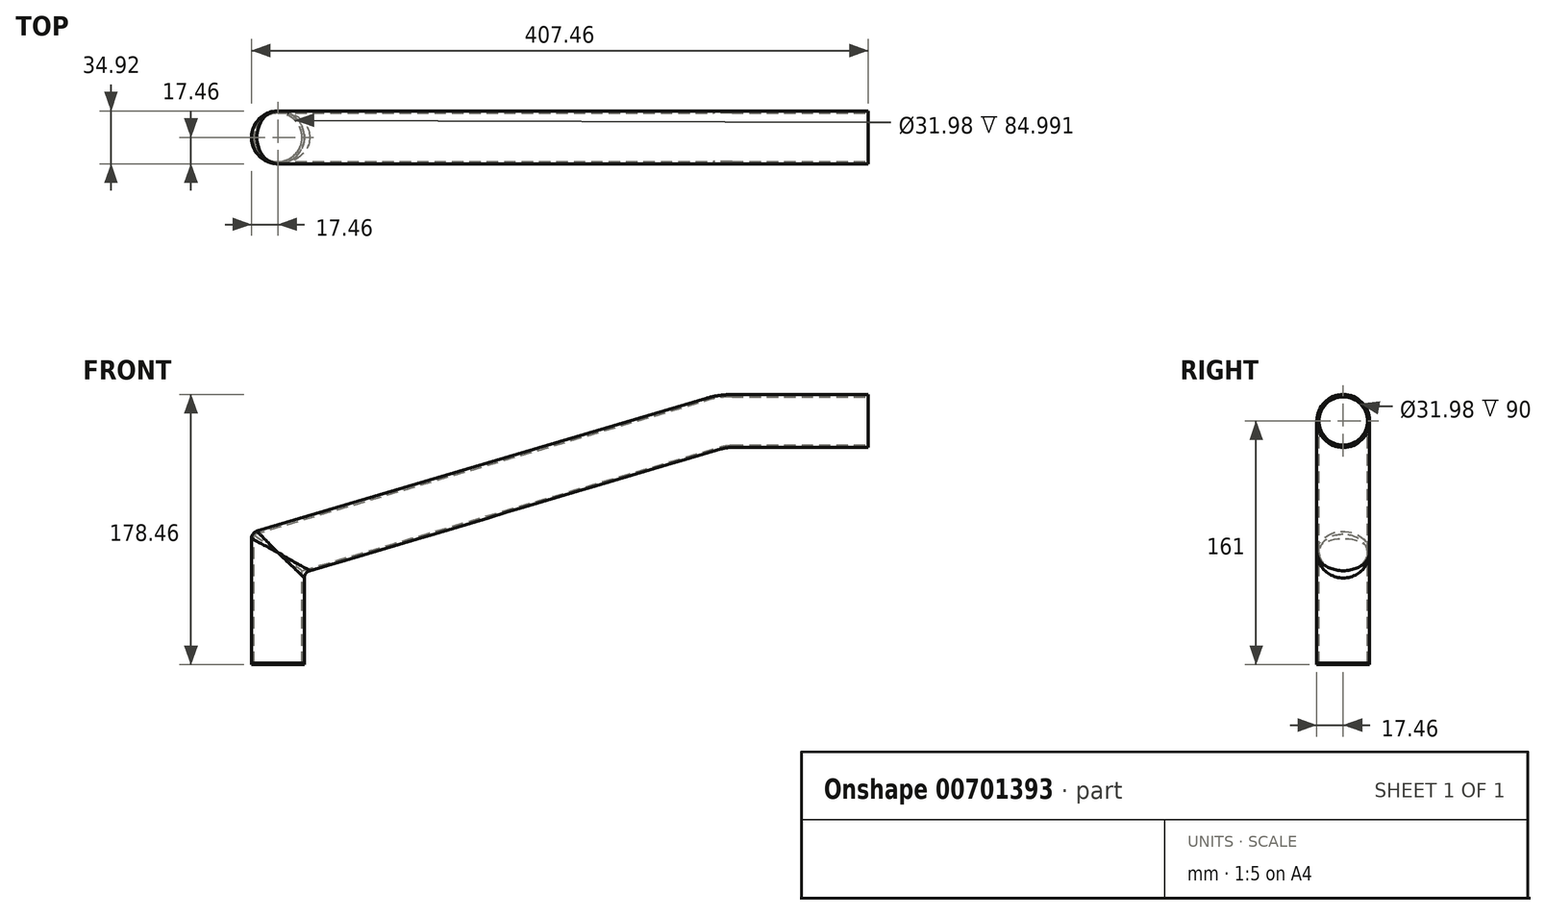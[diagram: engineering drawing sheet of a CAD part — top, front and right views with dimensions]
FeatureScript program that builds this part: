
annotation { "Feature Type Name" : "Feature", "Feature Type Description" : "" }
export const myFeature = defineFeature(function(context is Context, id is Id, definition is map)
    precondition{}
    {
        {
            var Q0;
            Q0=qCreatedBy(makeId("Front.planeOp"),FACE);
            var sketch = newSketch(context, id + "F0", { "sketchPlane" : qUnion([Q0])});
            skLineSegment(sketch, "E0", {"start": v(0, 0) * mm, "end": v(0, 73.04) * mm});
            skLineSegment(sketch, "E1", {"start": v(300, 160) * mm, "end": v(390, 160) * mm});
            skPoint(sketch, "E2.visualSharp", {"position": v(0, 160) * mm});
            skLineSegment(sketch, "E3", {"start": v(287.84, 158.24) * mm, "end": v(0, 73.04) * mm});
            skPoint(sketch, "E4.visualSharp", {"position": v(0, 73.04) * mm});
            skPoint(sketch, "E5.visualSharp", {"position": v(293.79, 160) * mm});
            skArc(sketch, "E5.filletArc", {"start": v(300, 160) * mm, "mid": v(293.85, 159.56) * mm, "end": v(287.84, 158.24) * mm});
            skLineSegment(sketch, "E6", {"start": v(293.79, 160) * mm, "end": v(0, 160) * mm, "construction": true});
            skLineSegment(sketch, "E7", {"start": v(0, 73.04) * mm, "end": v(0, 160) * mm, "construction": true});
            skLineSegment(sketch, "E8.0", {"start": v(17.46, 0) * mm, "end": v(17.46, 60) * mm});
            skLineSegment(sketch, "E8.1", {"start": v(300, 142.54) * mm, "end": v(390, 142.54) * mm});
            skArc(sketch, "E8.2", {"start": v(300, 142.54) * mm, "mid": v(296.36, 142.28) * mm, "end": v(292.8, 141.5) * mm});
            skLineSegment(sketch, "E8.3", {"start": v(292.8, 141.5) * mm, "end": v(17.46, 60) * mm});
            skSolve(sketch);
        }
        {
            var Q0;
            Q0=qCreatedBy(makeId("Top.planeOp"),FACE);
            var sketch = newSketch(context, id + "F1", { "sketchPlane" : qUnion([Q0])});
            skCircle(sketch, "E9", {"center": v(0, 0) * mm, "radius": 15.99 * mm});
            skCircle(sketch, "E10", {"center": v(0, 0) * mm, "radius": 17.46 * mm});
            skSolve(sketch);
        }
        {
            var Q0;
            Q0=makeQuery(id+"F1.imprint","IMPRINT",FACE,{"disambiguationData":[TD([[makeQuery(id+"F1.imprint","IMPRINT",EDGE,{"derivedFrom":sQuery(id+"F1.wireOp",EDGE,"E9")}),-1.0]])]});
            var Q1;
            Q1=sQuery(id+"F0.wireOp",EDGE,"E0");
            var Q2;
            Q2=sQuery(id+"F0.wireOp",EDGE,"E1");
            var Q3;
            Q3=sQuery(id+"F0.wireOp",EDGE,"E2.filletArc");
            var Q4;
            Q4=sQuery(id+"F0.wireOp",EDGE,"E3");
            var Q5;
            Q5=sQuery(id+"F0.wireOp",EDGE,"E5.filletArc");
            var Q6;
            Q6=sQuery(id+"F0.wireOp",EDGE,"E4.filletArc");
            sweep(context, id + "F2", {"profiles" : qUnion([Q0]), "path" : qUnion([Q1, Q2, Q3, Q4, Q5, Q6])});
        }
        {
            var Q0;
            Q0=makeQuery(id+"F1.imprint","IMPRINT",FACE,{"disambiguationData":[TD([[makeQuery(id+"F1.imprint","IMPRINT",EDGE,{"derivedFrom":sQuery(id+"F1.wireOp",EDGE,"E9")}),-1.0]])]});
            var Q1;
            Q1=makeQuery(id+"F1.imprint","IMPRINT",FACE,{"disambiguationData":[TD([[makeQuery(id+"F1.imprint","IMPRINT",EDGE,{"derivedFrom":sQuery(id+"F1.wireOp",EDGE,"E9")}),1.0]])]});
            extrude(context, id + "F3", {"entities" : qUnion([Q0, Q1]), "oppositeDirection" : true, "depth" : 1 * mm, "offsetDistance" : 25 * mm});
        }
        {
            var Q0;
            Q0=makeQuery(id+"F2.opSweep","MID_CAP_EDGE",EDGE,{"disambiguationData":[OSD([sQuery(id+"F0.wireOp",VERTEX,"E3.end"),sQuery(id+"F1.wireOp",EDGE,"E10")])],"capPos":1.0});
            fillet(context, id + "F4", {"entities" : qUnion([Q0]), "radius" : 5 * mm, "tangentPropagation" : true, "allowEdgeOverflow" : false});
        }
    });
